# Revit family: AD-S402T - Face-Based
name_source: partatom
category: Generic Models
revit_build: Autodesk Revit 2017 (Build: 20190508_0315(x64)
units: mm (PartAtom-declared; Revit-internal decimal feet)

## family parameters
Can host rebar = No
Cut with Voids When Loaded = No
Host = Face
Part Type = Normal
Room Calculation Point = No
Round Connector Dimension = Use Diameter
Shared = No

## types (3) — shared parameters
100V Taps = 60, 30, 15, 16 Ohm Bypass
70V Taps = 30, 15, 7.5, 16 Ohm Bypass
Coverage Horizontal = 150.00°
Coverage Vertical = 35.00°
Default Elevation = 4' - 0"
Depth = 0' - 4 31/32"
Description = 2.75" (x4) Columnar Surface-mount Loudspeaker
Height = 1' - 0 7/8"
Manufacturer = QSC
Manufacturer URL = https://www.qsc.com
Model = AD-S402T
Product Documentation Link = https://www.qsc.com
Product Page URL = https://www.qsc.com
Regulatory Compliance = UL1480A
SPL Max = 111
Sensitivity = 85
Weight Dimensional (kg) = 5
Weight Dimensional (lb) = 11
Weight Product (kg) = 3.4
Weight Product (lb) = 7.5
Width = 0' - 5 5/32"

## per-type parameters (varying)
| type | Mount Position |
| Mount Position 1 | AD-S402T - Layer 3 - Bracket : Mount Position 1 |
| Mount Position 2 | AD-S402T - Layer 3 - Bracket : Mount Position 2 |
| Mount Position 3 | AD-S402T - Layer 3 - Bracket : Mount Position 3 |

## geometry (parser evidence)
native form markers: Blend x4, Sweep x7
no freeform markers — native parametric forms only
